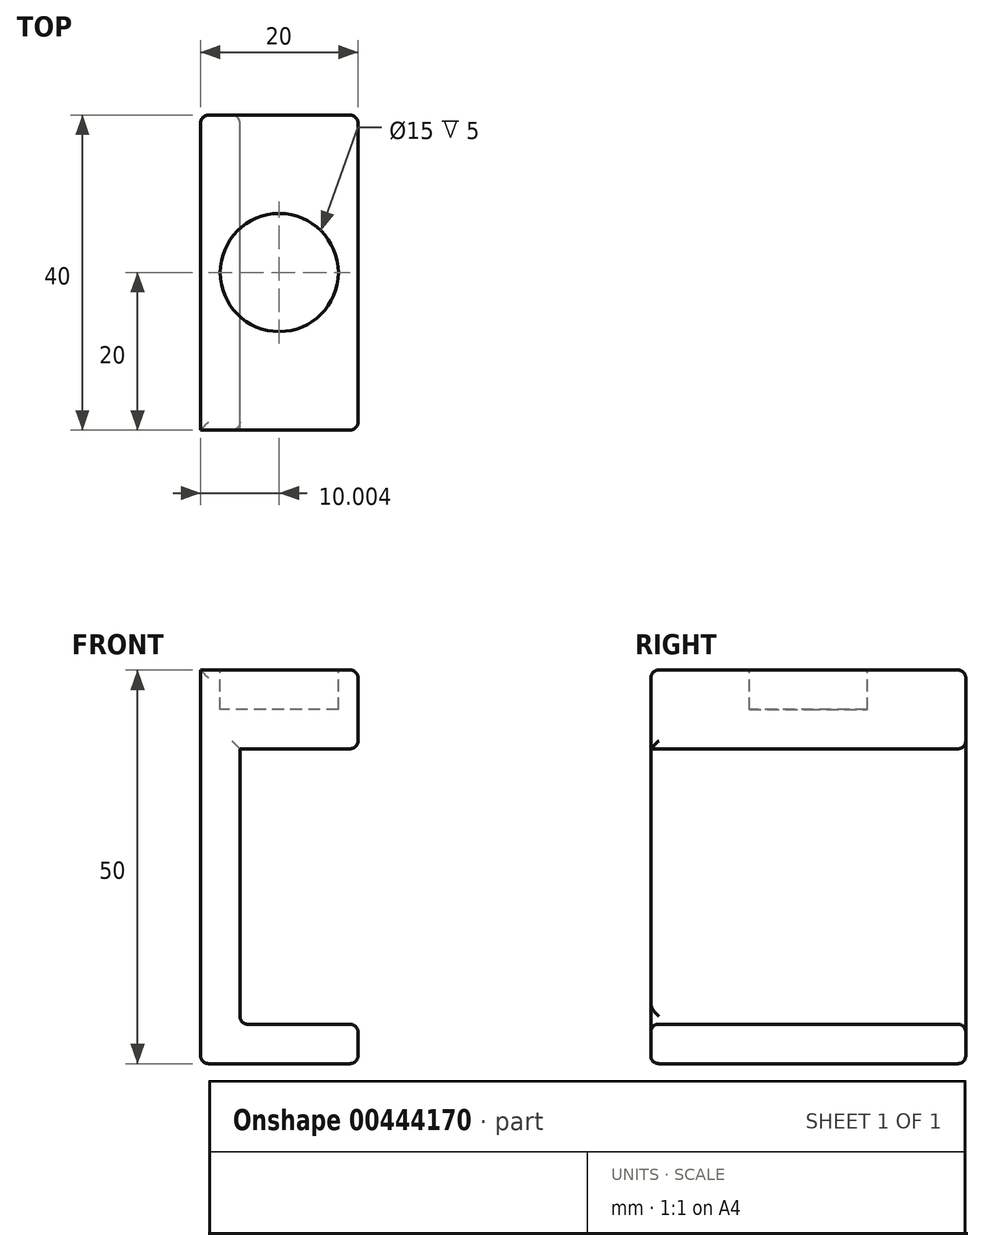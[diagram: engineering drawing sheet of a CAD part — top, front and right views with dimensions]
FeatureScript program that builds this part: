
annotation { "Feature Type Name" : "Feature", "Feature Type Description" : "" }
export const myFeature = defineFeature(function(context is Context, id is Id, definition is map)
    precondition{}
    {
        {
            var Q0;
            Q0=qCreatedBy(makeId("Front.planeOp"),FACE);
            var sketch = newSketch(context, id + "F0", { "sketchPlane" : qUnion([Q0])});
            skLineSegment(sketch, "E0", {"start": v(-32.13, 49.31) * mm, "end": v(-32.13, -0.69) * mm});
            skLineSegment(sketch, "E1", {"start": v(-32.13, -0.69) * mm, "end": v(-12.13, -0.69) * mm});
            skLineSegment(sketch, "E2", {"start": v(-12.13, -0.69) * mm, "end": v(-12.13, 4.31) * mm});
            skLineSegment(sketch, "E3", {"start": v(-12.13, 4.31) * mm, "end": v(-27.13, 4.31) * mm});
            skLineSegment(sketch, "E4", {"start": v(-27.13, 4.31) * mm, "end": v(-27.13, 39.31) * mm});
            skLineSegment(sketch, "E5", {"start": v(-27.13, 39.31) * mm, "end": v(-12.13, 39.31) * mm});
            skLineSegment(sketch, "E6", {"start": v(-12.13, 39.31) * mm, "end": v(-12.13, 49.31) * mm});
            skLineSegment(sketch, "E7", {"start": v(-12.13, 49.31) * mm, "end": v(-32.13, 49.31) * mm});
            skSolve(sketch);
        }
        {
            var Q0;
            Q0=makeQuery(id+"F0.imprint","IMPRINT",FACE,{"disambiguationData":[TD([[makeQuery(id+"F0.imprint","IMPRINT",EDGE,{"derivedFrom":sQuery(id+"F0.wireOp",EDGE,"E0")}),1.0]])]});
            extrude(context, id + "F1", {"entities" : qUnion([Q0]), "depth" : 40 * mm});
        }
        {
            var Q0;
            Q0=makeQuery(id+"F1.opExtrude","SWEPT_FACE",FACE,{"disambiguationData":[OSD([sQuery(id+"F0.wireOp",EDGE,"E7")])]});
            var sketch = newSketch(context, id + "F2", { "sketchPlane" : qUnion([Q0])});
            skCircle(sketch, "E8", {"center": v(-22.13, -20) * mm, "radius": 7.5 * mm});
            skSolve(sketch);
        }
        {
            var Q0;
            Q0=makeQuery(id+"F2.imprint","IMPRINT",FACE,{"disambiguationData":[TD([[makeQuery(id+"F2.imprint","IMPRINT",EDGE,{"derivedFrom":sQuery(id+"F2.wireOp",EDGE,"E8")}),1.0]])]});
            extrude(context, id + "F3", {"entities" : qUnion([Q0]), "operationType" : NewBodyOperationType.REMOVE, "oppositeDirection" : true, "depth" : 5 * mm});
        }
        {
            var Q0;
            Q0=makeQuery(id+"F1.opExtrude","CAP_EDGE",EDGE,{"disambiguationData":[OSD([sQuery(id+"F0.wireOp",EDGE,"E7")])],"isStart":false});
            var Q1;
            Q1=makeQuery(id+"F1.opExtrude","SWEPT_FACE",FACE,{"disambiguationData":[OSD([sQuery(id+"F0.wireOp",EDGE,"E6")])]});
            var Q2;
            Q2=makeQuery(id+"F1.opExtrude","CAP_FACE",FACE,{"disambiguationData":[OSD([sQuery(id+"F0.wireOp",EDGE,"E0"),sQuery(id+"F0.wireOp",EDGE,"E1"),sQuery(id+"F0.wireOp",EDGE,"E2"),sQuery(id+"F0.wireOp",EDGE,"E3"),sQuery(id+"F0.wireOp",EDGE,"E4"),sQuery(id+"F0.wireOp",EDGE,"E5"),sQuery(id+"F0.wireOp",EDGE,"E6"),sQuery(id+"F0.wireOp",EDGE,"E7")])],"isStart":true});
            var Q3;
            Q3=makeQuery(id+"F1.opExtrude","SWEPT_FACE",FACE,{"disambiguationData":[OSD([sQuery(id+"F0.wireOp",EDGE,"E3")])]});
            var Q4;
            Q4=makeQuery(id+"F1.opExtrude","SWEPT_FACE",FACE,{"disambiguationData":[OSD([sQuery(id+"F0.wireOp",EDGE,"E1")])]});
            var Q5;
            Q5=makeQuery(id+"F1.opExtrude","CAP_EDGE",EDGE,{"disambiguationData":[OSD([sQuery(id+"F0.wireOp",EDGE,"E2")])],"isStart":false});
            fillet(context, id + "F4", {"entities" : qUnion([Q0, Q1, Q2, Q3, Q4, Q5]), "radius" : 1 * mm, "tangentPropagation" : true, "allowEdgeOverflow" : false});
        }
    });
